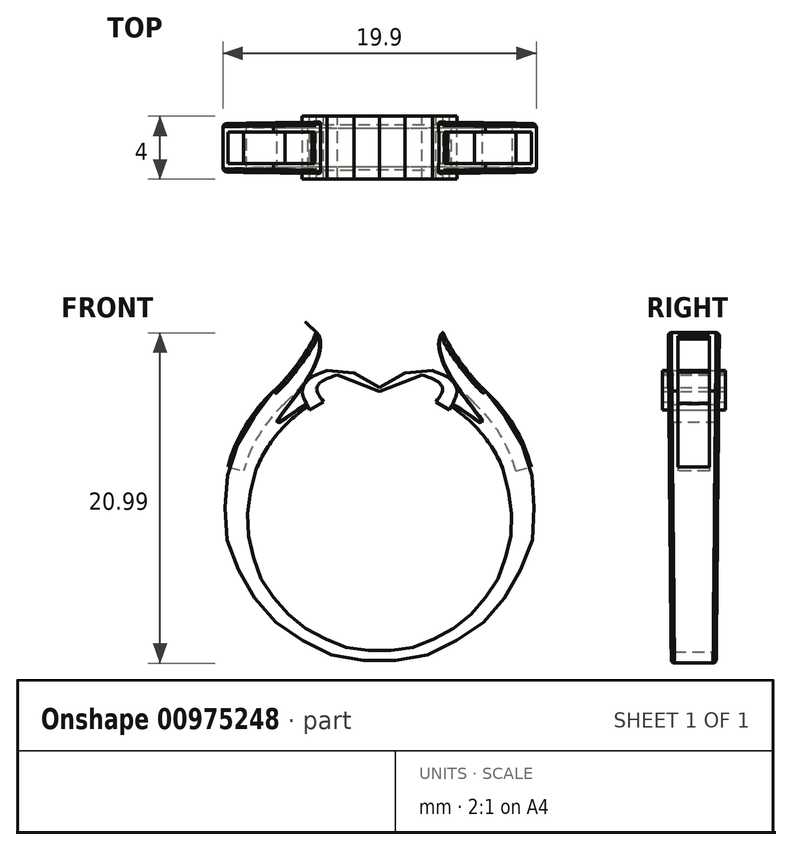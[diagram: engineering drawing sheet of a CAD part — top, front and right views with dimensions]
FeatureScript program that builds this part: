
annotation { "Feature Type Name" : "Feature", "Feature Type Description" : "" }
export const myFeature = defineFeature(function(context is Context, id is Id, definition is map)
    precondition{}
    {
        {
            var Q0;
            Q0=qCreatedBy(makeId("Front.planeOp"),FACE);
            var sketch = newSketch(context, id + "F0", { "sketchPlane" : qUnion([Q0])});
            skArc(sketch, "E0", {"start": v(-6.73, 8.12) * mm, "mid": v(0, -9.16) * mm, "end": v(6.73, 8.12) * mm});
            skArc(sketch, "E1", {"start": v(-4.55, 7.12) * mm, "mid": v(0, -8.45) * mm, "end": v(4.55, 7.12) * mm});
            skFitSpline(sketch, "E2", {"points": [v(-6.73, 8.12) * mm, v(-5.1, 10.01) * mm, v(-4.03, 11.86) * mm], "startDerivative": vector(3.3, 2.81) * mm, "endDerivative": vector(1.57, 4.42) * mm});
            skFitSpline(sketch, "E3", {"points": [v(-4.03, 11.86) * mm, v(-3.8, 11.54) * mm, v(-4.3, 9.33) * mm, v(-6.5, 6.11) * mm, v(-4.96, 7.12) * mm, v(-4.55, 7.12) * mm], "startDerivative": vector(2.68, -2.55) * mm, "endDerivative": vector(1.26, -4.37) * mm});
            skFitSpline(sketch, "E4.MirrorCS", {"points": [v(6.73, 8.12) * mm, v(5.1, 10.01) * mm, v(4.03, 11.86) * mm], "startDerivative": vector(-3.3, 2.81) * mm, "endDerivative": vector(-1.57, 4.42) * mm});
            skFitSpline(sketch, "E5.MirrorCS", {"points": [v(4.03, 11.86) * mm, v(3.8, 11.54) * mm, v(4.3, 9.33) * mm, v(6.5, 6.11) * mm, v(4.96, 7.12) * mm, v(4.55, 7.12) * mm], "startDerivative": vector(-2.68, -2.55) * mm, "endDerivative": vector(-1.26, -4.37) * mm});
            skSolve(sketch);
        }
        {
            var Q0;
            Q0=qSketchRegion(id+"F0",true);
            extrude(context, id + "F1", {"entities" : qUnion([Q0]), "endBound" : BoundingType.SYMMETRIC, "depth" : 3.25 * mm, "offsetDistance" : 25 * mm});
        }
        {
            var Q0;
            Q0=qCreatedBy(makeId("Right.planeOp"),FACE);
            var sketch = newSketch(context, id + "F2", { "sketchPlane" : qUnion([Q0])});
            skLineSegment(sketch, "E6", {"start": v(-1.64, 13.94) * mm, "end": v(-1.4, -12.17) * mm});
            skLineSegment(sketch, "E7", {"start": v(-1.4, -12.16) * mm, "end": v(-6.23, -12.16) * mm});
            skLineSegment(sketch, "E8", {"start": v(-6.23, -12.17) * mm, "end": v(-1.64, 13.94) * mm});
            skLineSegment(sketch, "E9.MirrorCS", {"start": v(1.64, 13.94) * mm, "end": v(1.4, -12.17) * mm});
            skLineSegment(sketch, "E10.MirrorCS", {"start": v(1.4, -12.16) * mm, "end": v(6.23, -12.16) * mm});
            skLineSegment(sketch, "E11.MirrorCS", {"start": v(6.23, -12.17) * mm, "end": v(1.64, 13.94) * mm});
            skSolve(sketch);
        }
        {
            var Q0;
            Q0=qSketchRegion(id+"F2",true);
            extrude(context, id + "F3", {"entities" : qUnion([Q0]), "operationType" : NewBodyOperationType.REMOVE, "endBound" : BoundingType.SYMMETRIC, "oppositeDirection" : true, "depth" : 25 * mm, "offsetDistance" : 25 * mm});
        }
        {
            var Q0;
            Q0=makeQuery(id+"F3.boolean.opBoolean","INTERSECT",EDGE,{"derivedFrom":[makeQuery(id+"F1.opExtrude","SWEPT_FACE",FACE,{"disambiguationData":[OSD([sQuery(id+"F0.wireOp",EDGE,"E1")])]}),makeQuery(id+"F3.opExtrude","SWEPT_FACE",FACE,{"disambiguationData":[OSD([sQuery(id+"F2.wireOp",EDGE,"E6")])]})]});
            var Q1;
            Q1=makeQuery(id+"F3.boolean.opBoolean","INTERSECT",EDGE,{"derivedFrom":[makeQuery(id+"F1.opExtrude","SWEPT_FACE",FACE,{"disambiguationData":[OSD([sQuery(id+"F0.wireOp",EDGE,"E1")])]}),makeQuery(id+"F3.opExtrude","SWEPT_FACE",FACE,{"disambiguationData":[OSD([sQuery(id+"F2.wireOp",EDGE,"E9.MirrorCS")])]})]});
            var Q2;
            Q2=makeQuery(id+"F3.boolean.opBoolean","INTERSECT",EDGE,{"derivedFrom":[makeQuery(id+"F1.opExtrude","SWEPT_FACE",FACE,{"disambiguationData":[OSD([sQuery(id+"F0.wireOp",EDGE,"E0")])]}),makeQuery(id+"F3.opExtrude","SWEPT_FACE",FACE,{"disambiguationData":[OSD([sQuery(id+"F2.wireOp",EDGE,"E6")])]})]});
            var Q3;
            Q3=makeQuery(id+"F3.boolean.opBoolean","INTERSECT",EDGE,{"derivedFrom":[makeQuery(id+"F1.opExtrude","SWEPT_FACE",FACE,{"disambiguationData":[OSD([sQuery(id+"F0.wireOp",EDGE,"E0")])]}),makeQuery(id+"F3.opExtrude","SWEPT_FACE",FACE,{"disambiguationData":[OSD([sQuery(id+"F2.wireOp",EDGE,"E9.MirrorCS")])]})]});
            fillet(context, id + "F4", {"entities" : qUnion([Q0, Q1, Q2, Q3]), "radius" : 0.2 * mm, "tangentPropagation" : true, "allowEdgeOverflow" : false});
        }
        {
            var Q0;
            Q0=makeQuery(id+"F1.opExtrude","SWEPT_EDGE",EDGE,{"disambiguationData":[OSD([sQuery(id+"F0.wireOp",EDGE,"E1"),sQuery(id+"F0.wireOp",EDGE,"E5.MirrorCS")])]});
            var Q1;
            Q1=makeQuery(id+"F1.opExtrude","SWEPT_EDGE",EDGE,{"disambiguationData":[OSD([sQuery(id+"F0.wireOp",EDGE,"E1"),sQuery(id+"F0.wireOp",EDGE,"E3")])]});
            fillet(context, id + "F5", {"entities" : qUnion([Q0, Q1]), "radius" : 0.05 * mm, "tangentPropagation" : true, "allowEdgeOverflow" : false});
        }
        {
            var Q0;
            Q0=qCreatedBy(makeId("Front.planeOp"),FACE);
            var sketch = newSketch(context, id + "F6", { "sketchPlane" : qUnion([Q0])});
            skLineSegment(sketch, "E12", {"start": v(-4.44, 6.9) * mm, "end": v(-3.58, 7.44) * mm});
            skFitSpline(sketch, "E13", {"points": [v(-4.44, 6.9) * mm, v(-4.92, 8.07) * mm, v(-4.54, 8.83) * mm, v(-3.34, 9.42) * mm], "startDerivative": vector(-1.27, 3.16) * mm, "endDerivative": vector(5.24, 1.8) * mm});
            skFitSpline(sketch, "E14", {"points": [v(-3.58, 7.44) * mm, v(-3.99, 8.17) * mm, v(-3.86, 8.57) * mm, v(-2.68, 9.14) * mm], "startDerivative": vector(-2.37, 3.4) * mm, "endDerivative": vector(3.42, 1.09) * mm});
            skLineSegment(sketch, "E15", {"start": v(-3.34, 9.42) * mm, "end": v(-1.62, 9.27) * mm});
            skLineSegment(sketch, "E16", {"start": v(-1.62, 9.27) * mm, "end": v(0, 8.35) * mm});
            skLineSegment(sketch, "E17", {"start": v(-2.68, 9.14) * mm, "end": v(0, 8.1) * mm});
            skLineSegment(sketch, "E18.MirrorCS", {"start": v(4.44, 6.9) * mm, "end": v(3.58, 7.44) * mm});
            skFitSpline(sketch, "E19.MirrorCS", {"points": [v(4.44, 6.9) * mm, v(4.92, 8.07) * mm, v(4.54, 8.83) * mm, v(3.34, 9.42) * mm], "startDerivative": vector(1.27, 3.16) * mm, "endDerivative": vector(-5.24, 1.8) * mm});
            skFitSpline(sketch, "E20.MirrorCS", {"points": [v(3.58, 7.44) * mm, v(3.99, 8.17) * mm, v(3.86, 8.57) * mm, v(2.68, 9.14) * mm], "startDerivative": vector(2.37, 3.4) * mm, "endDerivative": vector(-3.42, 1.09) * mm});
            skLineSegment(sketch, "E21.MirrorCS", {"start": v(2.68, 9.14) * mm, "end": v(0, 8.1) * mm});
            skLineSegment(sketch, "E22.MirrorCS", {"start": v(1.62, 9.27) * mm, "end": v(0, 8.35) * mm});
            skLineSegment(sketch, "E23.MirrorCS", {"start": v(3.34, 9.42) * mm, "end": v(1.62, 9.27) * mm});
            skSolve(sketch);
        }
        {
            var Q0;
            Q0 = qSketchRegion(id + "F6", true);
            extrude(context, id + "F7", {"entities" : qUnion([Q0]), "endBound" : BoundingType.SYMMETRIC, "depth" : 4 * mm, "offsetDistance" : 25 * mm});
        }
        {
            var Q0;
            Q0=qCreatedBy(makeId("Top.planeOp"),FACE);
            cPlane(context, id + "F8", {"entities" : qUnion([Q0]), "cplaneType" : CPlaneType.OFFSET, "offset" : 0.71 * mm, "width" : 150 * mm, "height" : 150 * mm});
        }
        {
            var Q0;
            Q0=qCreatedBy(id+"F8.planeOp",FACE);
            var sketch = newSketch(context, id + "F9", { "sketchPlane" : qUnion([Q0])});
            skLineSegment(sketch, "E24", {"start": v(0, 6.65) * mm, "end": v(0, -5.87) * mm, "construction": true});
            skSolve(sketch);
        }
        {
            var Q0;
            Q0=sQuery(id+"F9.wireOp",EDGE,"E24");
            var Q1;
            Q1=qCreatedBy(id+"F8.planeOp",FACE);
            cPlane(context, id + "F10", {"entities" : qUnion([Q0, Q1]), "cplaneType" : CPlaneType.LINE_ANGLE, "offset" : 25 * mm, "angle" : 15 * degree, "oppositeDirection" : true, "width" : 150 * mm, "height" : 150 * mm});
        }
        {
            var Q0;
            Q0=qCreatedBy(id+"F10.planeOp",FACE);
            var sketch = newSketch(context, id + "F11", { "sketchPlane" : qUnion([Q0])});
            skLineSegment(sketch, "E25.bottom", {"start": v(-11.14, -1) * mm, "end": v(-9.14, -1) * mm});
            skLineSegment(sketch, "E25.top", {"start": v(-11.14, 1) * mm, "end": v(-9.14, 1) * mm});
            skLineSegment(sketch, "E25.left", {"start": v(-11.14, -1) * mm, "end": v(-11.14, 1) * mm});
            skLineSegment(sketch, "E25.right", {"start": v(-9.14, -1) * mm, "end": v(-9.14, 1) * mm});
            skSolve(sketch);
        }
        {
            var Q0;
            Q0 = qSketchRegion(id + "F11", true);
            var Q1;
            Q1=sQuery(id+"F9.wireOp",EDGE,"E24");
            revolve(context, id + "F12", {"operationType" : NewBodyOperationType.REMOVE, "surfaceOperationType" : NewSurfaceOperationType.NEW, "entities" : qUnion([Q0]), "axis" : qUnion([Q1]), "revolveType" : RevolveType.ONE_DIRECTION, "oppositeDirection" : true, "angle" : 32.7 * degree});
        }
        {
            var Q0;
            Q0=qCreatedBy(id+"F8.planeOp",FACE);
            var Q1;
            Q1=sQuery(id+"F9.wireOp",EDGE,"E24");
            cPlane(context, id + "F13", {"entities" : qUnion([Q0, Q1]), "cplaneType" : CPlaneType.LINE_ANGLE, "offset" : 25 * mm, "angle" : 15 * degree, "width" : 150 * mm, "height" : 150 * mm});
        }
        {
            var Q0;
            Q0=qCreatedBy(id+"F13.planeOp",FACE);
            var sketch = newSketch(context, id + "F14", { "sketchPlane" : qUnion([Q0])});
            skLineSegment(sketch, "E26.bottom", {"start": v(9.14, -1) * mm, "end": v(11.14, -1) * mm});
            skLineSegment(sketch, "E26.top", {"start": v(9.14, 1) * mm, "end": v(11.14, 1) * mm});
            skLineSegment(sketch, "E26.left", {"start": v(9.14, -1) * mm, "end": v(9.14, 1) * mm});
            skLineSegment(sketch, "E26.right", {"start": v(11.14, -1) * mm, "end": v(11.14, 1) * mm});
            skSolve(sketch);
        }
        {
            var Q0;
            Q0=makeQuery(id+"F14.imprint","IMPRINT",FACE,{"disambiguationData":[TD([[makeQuery(id+"F14.imprint","IMPRINT",EDGE,{"derivedFrom":sQuery(id+"F14.wireOp",EDGE,"E26.bottom")}),1.0]])]});
            var Q1;
            Q1=sQuery(id+"F9.wireOp",EDGE,"E24");
            revolve(context, id + "F15", {"operationType" : NewBodyOperationType.REMOVE, "surfaceOperationType" : NewSurfaceOperationType.NEW, "entities" : qUnion([Q0]), "axis" : qUnion([Q1]), "revolveType" : RevolveType.ONE_DIRECTION, "angle" : 32.7 * degree});
        }
        {
            var Q0;
            Q0=qCreatedBy(makeId("Front.planeOp"),FACE);
            var sketch = newSketch(context, id + "F16", { "sketchPlane" : qUnion([Q0])});
            skFitSpline(sketch, "E27", {"points": [v(-6.73, 8.12) * mm, v(-5.97, 8.89) * mm, v(-5.37, 9.65) * mm, v(-4.8, 10.41) * mm, v(-4.37, 11.07) * mm, v(-4.12, 11.6) * mm], "startDerivative": vector(3.43, 3.52) * mm, "endDerivative": vector(1.74, 3.92) * mm});
            skFitSpline(sketch, "E28.MirrorCS", {"points": [v(6.73, 8.12) * mm, v(5.97, 8.89) * mm, v(5.37, 9.65) * mm, v(4.8, 10.41) * mm, v(4.37, 11.07) * mm, v(4.12, 11.6) * mm], "startDerivative": vector(-3.43, 3.52) * mm, "endDerivative": vector(-1.74, 3.92) * mm});
            skSolve(sketch);
        }
        {
            var Q0;
            Q0=makeQuery(id+"F12.boolean.opBoolean","COPY",FACE,{"derivedFrom":makeQuery(id+"F12.opRevolve","CAP_FACE",FACE,{"disambiguationData":[OSD([sQuery(id+"F11.wireOp",EDGE,"E25.bottom"),sQuery(id+"F11.wireOp",EDGE,"E25.top"),sQuery(id+"F11.wireOp",EDGE,"E25.left"),sQuery(id+"F11.wireOp",EDGE,"E25.right")])],"isStart":false})});
            var sketch = newSketch(context, id + "F17", { "sketchPlane" : qUnion([Q0])});
            skLineSegment(sketch, "E29.bottom", {"start": v(-1, 11.11) * mm, "end": v(1, 11.11) * mm});
            skLineSegment(sketch, "E29.top", {"start": v(-1, 9.48) * mm, "end": v(1, 9.48) * mm});
            skLineSegment(sketch, "E29.left", {"start": v(-1, 11.11) * mm, "end": v(-1, 9.48) * mm});
            skLineSegment(sketch, "E29.right", {"start": v(1, 11.11) * mm, "end": v(1, 9.48) * mm});
            skSolve(sketch);
        }
        {
            var Q0;
            Q0 = qSketchRegion(id + "F17", true);
            var Q1;
            Q1=sQuery(id+"F16.wireOp",EDGE,"E27");
            sweep(context, id + "F18", {"operationType" : NewBodyOperationType.REMOVE, "profiles" : qUnion([Q0]), "path" : qUnion([Q1])});
        }
        {
            var Q0;
            Q0=makeQuery(id+"F15.boolean.opBoolean","COPY",FACE,{"derivedFrom":makeQuery(id+"F15.opRevolve","CAP_FACE",FACE,{"disambiguationData":[OSD([sQuery(id+"F14.wireOp",EDGE,"E26.bottom"),sQuery(id+"F14.wireOp",EDGE,"E26.top"),sQuery(id+"F14.wireOp",EDGE,"E26.left"),sQuery(id+"F14.wireOp",EDGE,"E26.right")])],"isStart":false})});
            var sketch = newSketch(context, id + "F19", { "sketchPlane" : qUnion([Q0])});
            skLineSegment(sketch, "E30.bottom", {"start": v(-1, 10.98) * mm, "end": v(1, 10.98) * mm});
            skLineSegment(sketch, "E30.top", {"start": v(-1, 9.48) * mm, "end": v(1, 9.48) * mm});
            skLineSegment(sketch, "E30.left", {"start": v(-1, 10.98) * mm, "end": v(-1, 9.48) * mm});
            skLineSegment(sketch, "E30.right", {"start": v(1, 10.98) * mm, "end": v(1, 9.48) * mm});
            skSolve(sketch);
        }
        {
            var Q0;
            Q0 = qSketchRegion(id + "F19", true);
            var Q1;
            Q1=sQuery(id+"F16.wireOp",EDGE,"E28.MirrorCS");
            sweep(context, id + "F20", {"operationType" : NewBodyOperationType.REMOVE, "profiles" : qUnion([Q0]), "path" : qUnion([Q1])});
        }
    });
